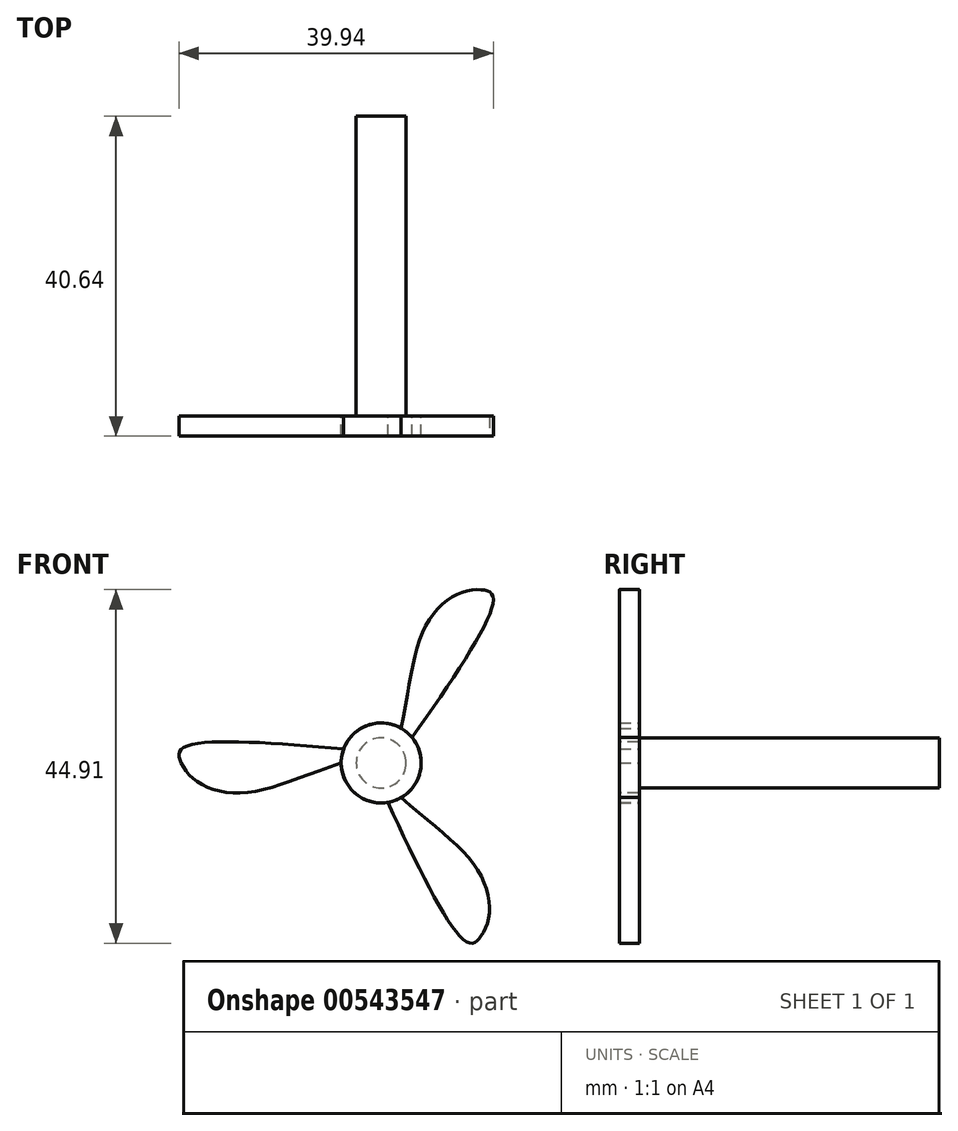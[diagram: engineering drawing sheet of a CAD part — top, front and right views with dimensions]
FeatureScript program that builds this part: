
annotation { "Feature Type Name" : "Feature", "Feature Type Description" : "" }
export const myFeature = defineFeature(function(context is Context, id is Id, definition is map)
    precondition{}
    {
        {
            var Q0;
            Q0=qCreatedBy(makeId("Front.planeOp"),FACE);
            var sketch = newSketch(context, id + "F0", { "sketchPlane" : qUnion([Q0])});
            skCircle(sketch, "E0", {"center": v(0, 0) * mm, "radius": 5.08 * mm});
            skLineSegment(sketch, "E1", {"start": v(-25.4, 0) * mm, "end": v(0, 0) * mm});
            skLineSegment(sketch, "E2", {"start": v(0, 0) * mm, "end": v(25.4, 0) * mm});
            skLineSegment(sketch, "E3", {"start": v(17.78, 18.62) * mm, "end": v(17.78, -16.85) * mm, "construction": true});
            skLineSegment(sketch, "E4", {"start": v(4.76, -1.78) * mm, "end": v(-33.8, -1.78) * mm, "construction": true});
            skLineSegment(sketch, "E5", {"start": v(-34.98, 1.78) * mm, "end": v(36.6, 1.78) * mm, "construction": true});
            skPoint(sketch, "E6.0.internal.snap0", {"position": v(-12.7, 0) * mm});
            skFitSpline(sketch, "E6", {"points": [v(-5.08, 0) * mm, v(-17.48, -3.8) * mm, v(-23.14, -2.52) * mm, v(-25.4, 0) * mm, v(-25.36, 1.78) * mm, v(-4.76, 1.78) * mm], "startDerivative": vector(-58.96, -20.12) * mm, "endDerivative": vector(85.7, -7.49) * mm});
            skSolve(sketch);
        }
        {
            var Q0;
            Q0 = qSketchRegion(id + "F0", true);
            extrude(context, id + "F1", {"entities" : qUnion([Q0]), "depth" : 2.54 * mm, "offsetDistance" : 25.4 * mm});
        }
        {
            var Q0;
            Q0=makeQuery(id+"F1.opExtrude","CAP_FACE",FACE,{"disambiguationData":[OSD([sQuery(id+"F0.wireOp",EDGE,"E0"),sQuery(id+"F0.wireOp",EDGE,"E6")])],"isStart":true});
            var sketch = newSketch(context, id + "F2", { "sketchPlane" : qUnion([Q0])});
            skCircle(sketch, "E7", {"center": v(0, 0) * mm, "radius": 3.18 * mm});
            skSolve(sketch);
        }
        {
            var Q0;
            Q0=makeQuery(id+"F2.imprint","IMPRINT",FACE,{"disambiguationData":[TD([[makeQuery(id+"F2.imprint","IMPRINT",EDGE,{"derivedFrom":sQuery(id+"F2.wireOp",EDGE,"E7")}),1.0]])]});
            extrude(context, id + "F3", {"entities" : qUnion([Q0]), "depth" : 38.1 * mm, "offsetDistance" : 25.4 * mm});
        }
        {
            var Q0;
            Q0=makeQuery(id+"F1.opExtrude","SWEPT_BODY",BODY,{"disambiguationData":[OSD([sQuery(id+"F0.wireOp",EDGE,"E0"),sQuery(id+"F0.wireOp",EDGE,"E6")])]});
            var Q1;
            Q1=makeQuery(id+"F3.opExtrude","SWEPT_FACE",FACE,{"disambiguationData":[OSD([sQuery(id+"F2.wireOp",EDGE,"E7")])]});
            circularPattern(context, id + "F4", {"entities" : qUnion([Q0]), "axis" : qUnion([Q1]), "angle" : 360 * degree, "instanceCount" : 3, "equalSpace" : true});
        }
    });
